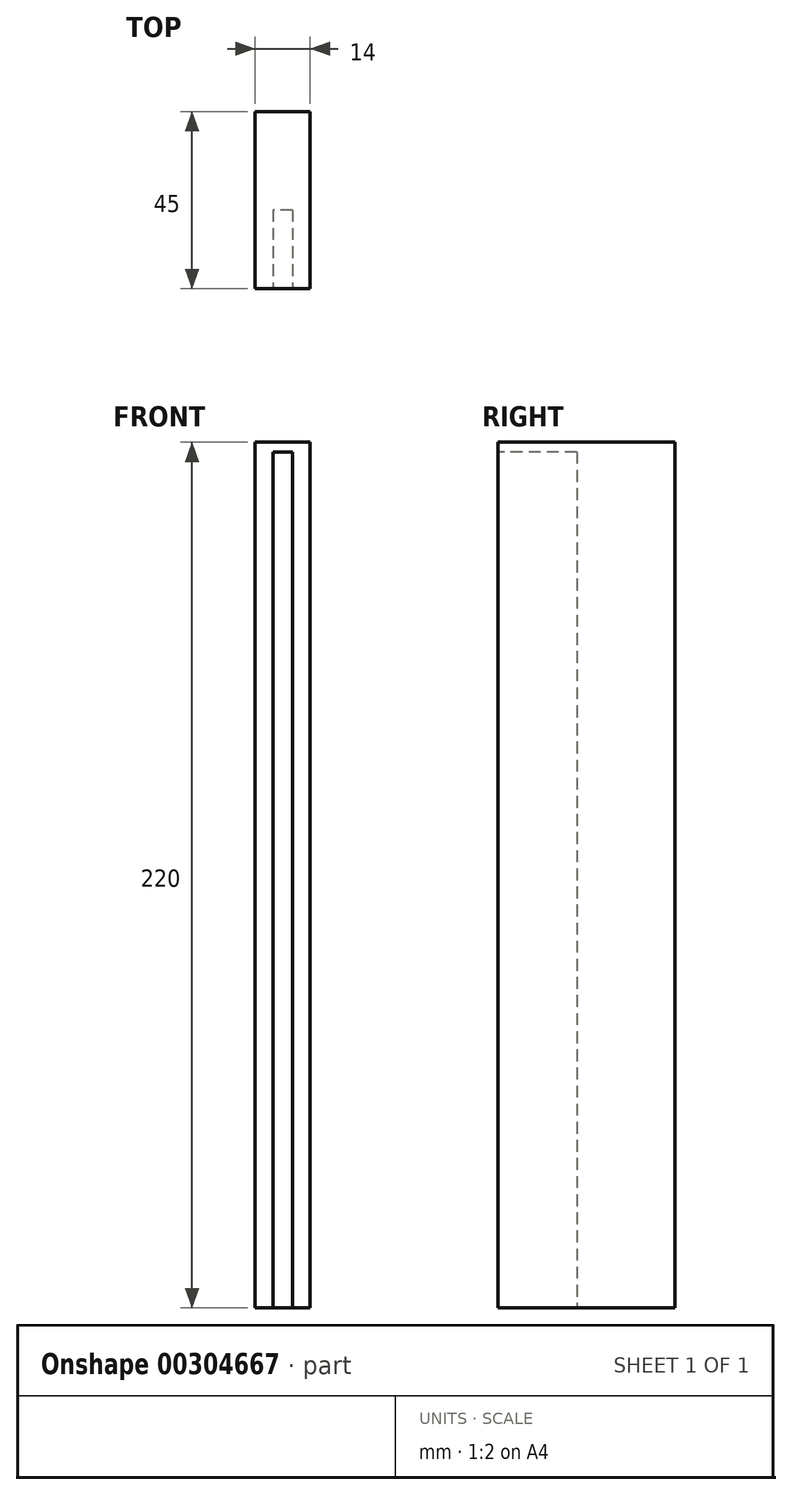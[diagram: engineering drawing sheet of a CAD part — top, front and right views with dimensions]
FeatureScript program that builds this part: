
annotation { "Feature Type Name" : "Feature", "Feature Type Description" : "" }
export const myFeature = defineFeature(function(context is Context, id is Id, definition is map)
    precondition{}
    {
        {
            var Q0;
            Q0=qCreatedBy(makeId("Right.planeOp"),FACE);
            var sketch = newSketch(context, id + "F0", { "sketchPlane" : qUnion([Q0])});
            skLineSegment(sketch, "E0.bottom", {"start": v(-13.7, -30.18) * mm, "end": v(31.3, -30.18) * mm});
            skLineSegment(sketch, "E0.top", {"start": v(-13.7, 189.82) * mm, "end": v(31.3, 189.82) * mm});
            skLineSegment(sketch, "E0.left", {"start": v(-13.7, -30.18) * mm, "end": v(-13.7, 189.82) * mm});
            skLineSegment(sketch, "E0.right", {"start": v(31.3, -30.18) * mm, "end": v(31.3, 189.82) * mm});
            skSolve(sketch);
        }
        {
            var Q0;
            Q0=qSketchRegion(id+"F0",true);
            extrude(context, id + "F1", {"entities" : qUnion([Q0]), "depth" : 7 * mm, "hasSecondDirection" : true, "secondDirectionOppositeDirection" : true, "secondDirectionDepth" : 7 * mm});
        }
        {
            var Q0;
            Q0=makeQuery(id+"F1.opExtrude","SWEPT_FACE",FACE,{"disambiguationData":[OSD([sQuery(id+"F0.wireOp",EDGE,"E0.left")])]});
            var sketch = newSketch(context, id + "F2", { "sketchPlane" : qUnion([Q0])});
            skLineSegment(sketch, "E1", {"start": v(0, 189.82) * mm, "end": v(0, 189.32) * mm, "construction": true});
            skPoint(sketch, "E2.endSnap0", {"position": v(0, -30.18) * mm});
            skLineSegment(sketch, "E3.bottom", {"start": v(-2.5, 187.32) * mm, "end": v(2.5, 187.32) * mm});
            skLineSegment(sketch, "E3.top", {"start": v(-2.5, -30.18) * mm, "end": v(2.5, -30.18) * mm});
            skLineSegment(sketch, "E3.left", {"start": v(-2.5, 187.32) * mm, "end": v(-2.5, -30.18) * mm});
            skLineSegment(sketch, "E3.right", {"start": v(2.5, 187.32) * mm, "end": v(2.5, -30.18) * mm});
            skSolve(sketch);
        }
        {
            var Q0;
            Q0=qSketchRegion(id+"F2",true);
            extrude(context, id + "F3", {"entities" : qUnion([Q0]), "operationType" : NewBodyOperationType.REMOVE, "oppositeDirection" : true, "depth" : 20 * mm});
        }
    });
